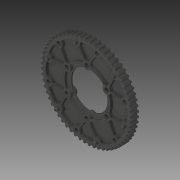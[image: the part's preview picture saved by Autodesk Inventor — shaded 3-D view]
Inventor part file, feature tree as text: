
AUTODESK INVENTOR PART (.ipt)
format: ipt  version: 2019 (Build 230136000, 136)  size: 1,587,712 bytes
history: native  units: in
note: dims shown in document units (in); Inventor stores cm internally (conversion verified against a paired STEP export)
features: fillet x1
ambient origin geometry x8: Origin, YZ Plane, XZ Plane, XY Plane, X Axis, Y Axis, Z Axis, Center Point
bodies: Solid1 (feature_tree)
feature tree (1):
  fillet  "Fillet3"  [1 undecoded]
note: 1 required parameter value undecoded (feature->parameter linkage not recoverable at this tier; creation-order binding heuristic only, values carry confidence <= 0.55)
